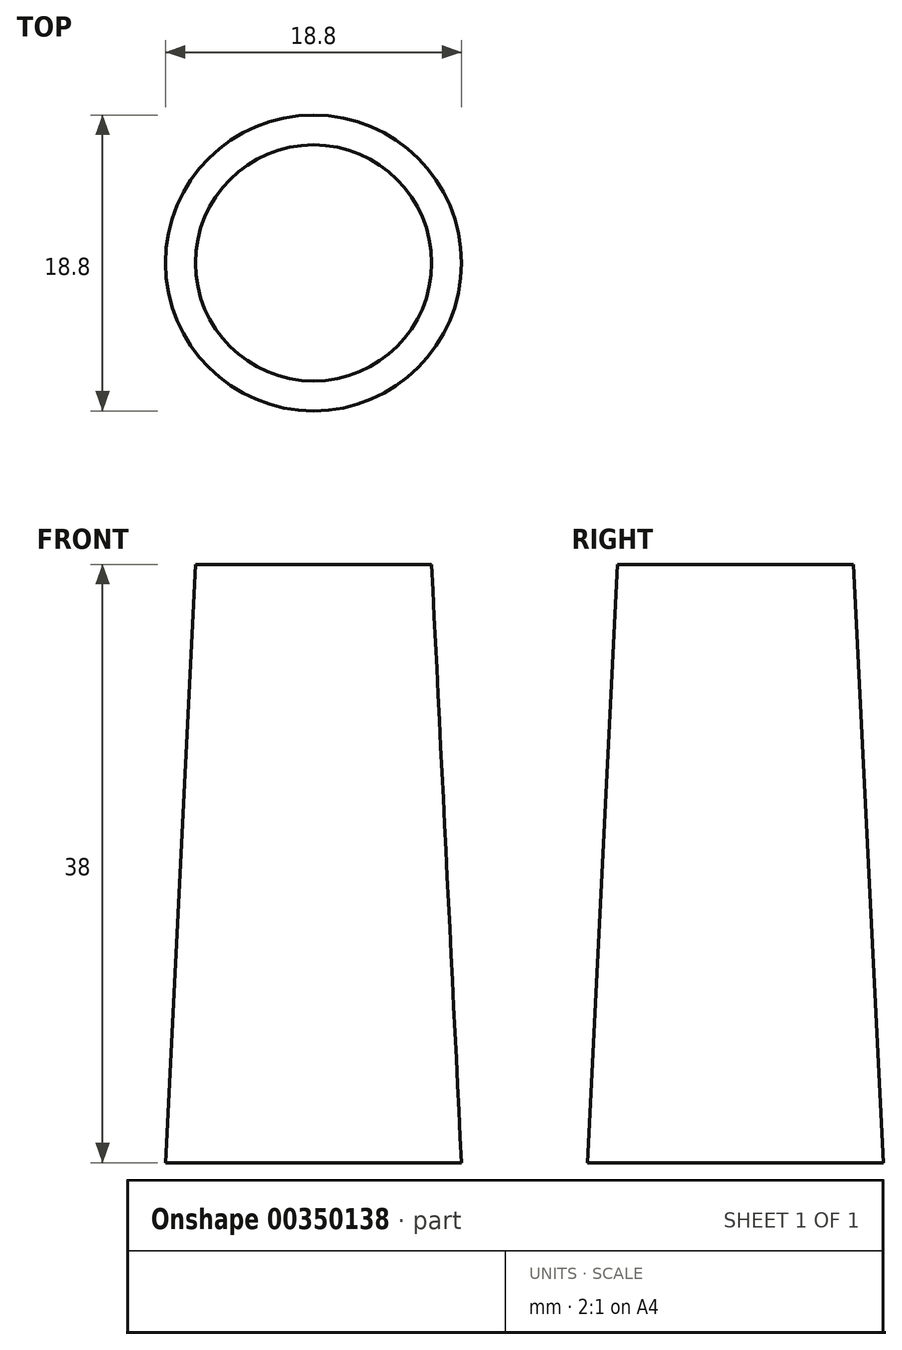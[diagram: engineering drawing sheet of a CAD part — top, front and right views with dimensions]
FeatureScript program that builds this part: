
annotation { "Feature Type Name" : "Feature", "Feature Type Description" : "" }
export const myFeature = defineFeature(function(context is Context, id is Id, definition is map)
    precondition{}
    {
        {
            var Q0;
            Q0=qCreatedBy(makeId("Top.planeOp"),FACE);
            cPlane(context, id + "F0", {"entities" : qUnion([Q0]), "cplaneType" : CPlaneType.OFFSET, "offset" : 38 * mm, "width" : 150 * mm, "height" : 150 * mm});
        }
        {
            var Q0;
            Q0=qCreatedBy(makeId("Top.planeOp"),FACE);
            var sketch = newSketch(context, id + "F1", { "sketchPlane" : qUnion([Q0])});
            skCircle(sketch, "E0", {"center": v(0, 0) * mm, "radius": 9.4 * mm});
            skSolve(sketch);
        }
        {
            var Q0;
            Q0=qCreatedBy(id+"F0.planeOp",FACE);
            var sketch = newSketch(context, id + "F2", { "sketchPlane" : qUnion([Q0])});
            skCircle(sketch, "E1", {"center": v(0, 0) * mm, "radius": 7.5 * mm});
            skSolve(sketch);
        }
        {
            var Q0;
            Q0=makeQuery(id+"F2.imprint","IMPRINT",FACE,{"disambiguationData":[TD([[makeQuery(id+"F2.imprint","IMPRINT",EDGE,{"derivedFrom":sQuery(id+"F2.wireOp",EDGE,"E1")}),1.0]])]});
            var Q1;
            Q1=makeQuery(id+"F1.imprint","IMPRINT",FACE,{"disambiguationData":[TD([[makeQuery(id+"F1.imprint","IMPRINT",EDGE,{"derivedFrom":sQuery(id+"F1.wireOp",EDGE,"E0")}),1.0]])]});
            loft(context, id + "F3", {"sheetProfilesArray" : [{ "sheetProfileEntities" : qUnion([Q0]) }, { "sheetProfileEntities" : qUnion([Q1]) }]});
        }
    });
